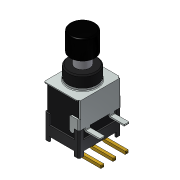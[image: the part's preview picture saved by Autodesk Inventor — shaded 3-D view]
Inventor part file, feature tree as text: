
AUTODESK INVENTOR PART (.ipt)
format: ipt  version: 2013 SP2 (Build 170200200, 200)  size: 551,936 bytes
history: native  units: mm
features: other x30, sketch x22, extrude x20, chamfer x4, fillet x3
ambient origin geometry x8: Origin, YZ Plane, XZ Plane, XY Plane, X Axis, Y Axis, Z Axis, Center Point
feature tree (79):
  extrude  "Vysunutí5"  Depth=7.2mm
  extrude  "Vysunutí6"  Depth=8.8mm
  extrude  "Vysunutí7"  Depth=5.0mm TaperAngle=0.0deg
  extrude  "Vysunutí8"  Depth=0.3mm
  extrude  "Vysunutí9"  Depth=13.9mm TaperAngle=0.0deg
  extrude  "Vysunutí10"  Depth=1.0mm
  extrude  "Vysunutí11"  Depth=1.0mm
  other  "Součást ohnutí1"
  extrude  "Vysunutí12"  Depth=2.0mm
  extrude  "Vysunutí13"  Depth=13.9mm TaperAngle=0.0deg
  extrude  "Vysunutí14"  Depth=2.0mm
  extrude  "Vysunutí15"  Depth=1.0mm
  fillet  "Zaoblení1"  Radius=1.0mm
  extrude  "Vysunutí16"  Depth=13.9mm TaperAngle=0.0deg
  extrude  "Vysunutí17"  Depth=10.2mm TaperAngle=0.0deg
  extrude  "Vysunutí18"  Depth=1.0mm TaperAngle=0.0deg
  chamfer  "Zkosení1"  Distance=0.6mm
  extrude  "Vysunutí19"  Depth=0.6mm
  extrude  "Vysunutí24"  Depth=30.0mm
  other  "Součást ohnutí2"
  fillet  "Zaoblení2"  Radius=1.5mm
  extrude  "Vysunutí20"  Depth=6.085mm TaperAngle=0.0deg
  chamfer  "Zkosení2"  Distance=0.9mm
  extrude  "Vysunutí21"  Depth=0.5mm TaperAngle=90.0deg
  chamfer  "Zkosení3"  Distance=0.3mm
  extrude  "Vysunutí22"  Depth=7.3mm
  fillet  "Zaoblení3"  Radius=0.3mm
  extrude  "Vysunutí25"  Depth=0.2mm TaperAngle=0.0deg
  chamfer  "Zkosení4"  Distance=5.2mm
  sketch  "Náčrt1"
  sketch  "Náčrt6"
  sketch  "Náčrt8"
  sketch  "Náčrt9"
  sketch  "Náčrt10"
  other  "Těleso6"
  sketch  "Náčrt11"
  sketch  "Náčrt13"
  other  "Těleso7"
  sketch  "Náčrt14"
  sketch  "Náčrt15"
  other  "Těleso8"
  sketch  "Náčrt16"
  sketch  "Náčrt17"
  sketch  "Náčrt18"
  sketch  "Náčrt19"
  sketch  "Náčrt20"
  sketch  "Náčrt21"
  sketch  "Náčrt22"
  sketch  "Náčrt23"
  sketch  "Náčrt24"
  other  "Těleso9"
  sketch  "Náčrt25"
  other  "Těleso10"
  sketch  "Náčrt27"
  sketch  "Náčrt28"
  sketch  "Náčrt29"
  other  "Promítnout říznuté hrany1"
  other  "Promítnout říznuté hrany2"
  other  "Promítnout říznuté hrany3"
  other  "Promítnout říznuté hrany4"
  other  "Promítnout říznuté hrany5"
  other  "Promítnout říznuté hrany7"
  other  "Promítnout říznuté hrany8"
  other  "Promítnout říznuté hrany9"
  other  "Promítnout říznuté hrany10"
  other  "Promítnout říznuté hrany11"
  other  "Promítnout říznuté hrany12"
  other  "Promítnout říznuté hrany13"
  other  "Promítnout říznuté hrany14"
  other  "Promítnout říznuté hrany15"
  other  "Promítnout říznuté hrany16"
  other  "Promítnout říznuté hrany17"
  other  "Promítnout říznuté hrany18"
  other  "Promítnout říznuté hrany19"
  other  "Promítnout říznuté hrany20"
  other  "Promítnout říznuté hrany21"
  other  "Promítnout říznuté hrany23"
  other  "Promítnout říznuté hrany24"
  other  "Promítnout říznuté hrany25"
